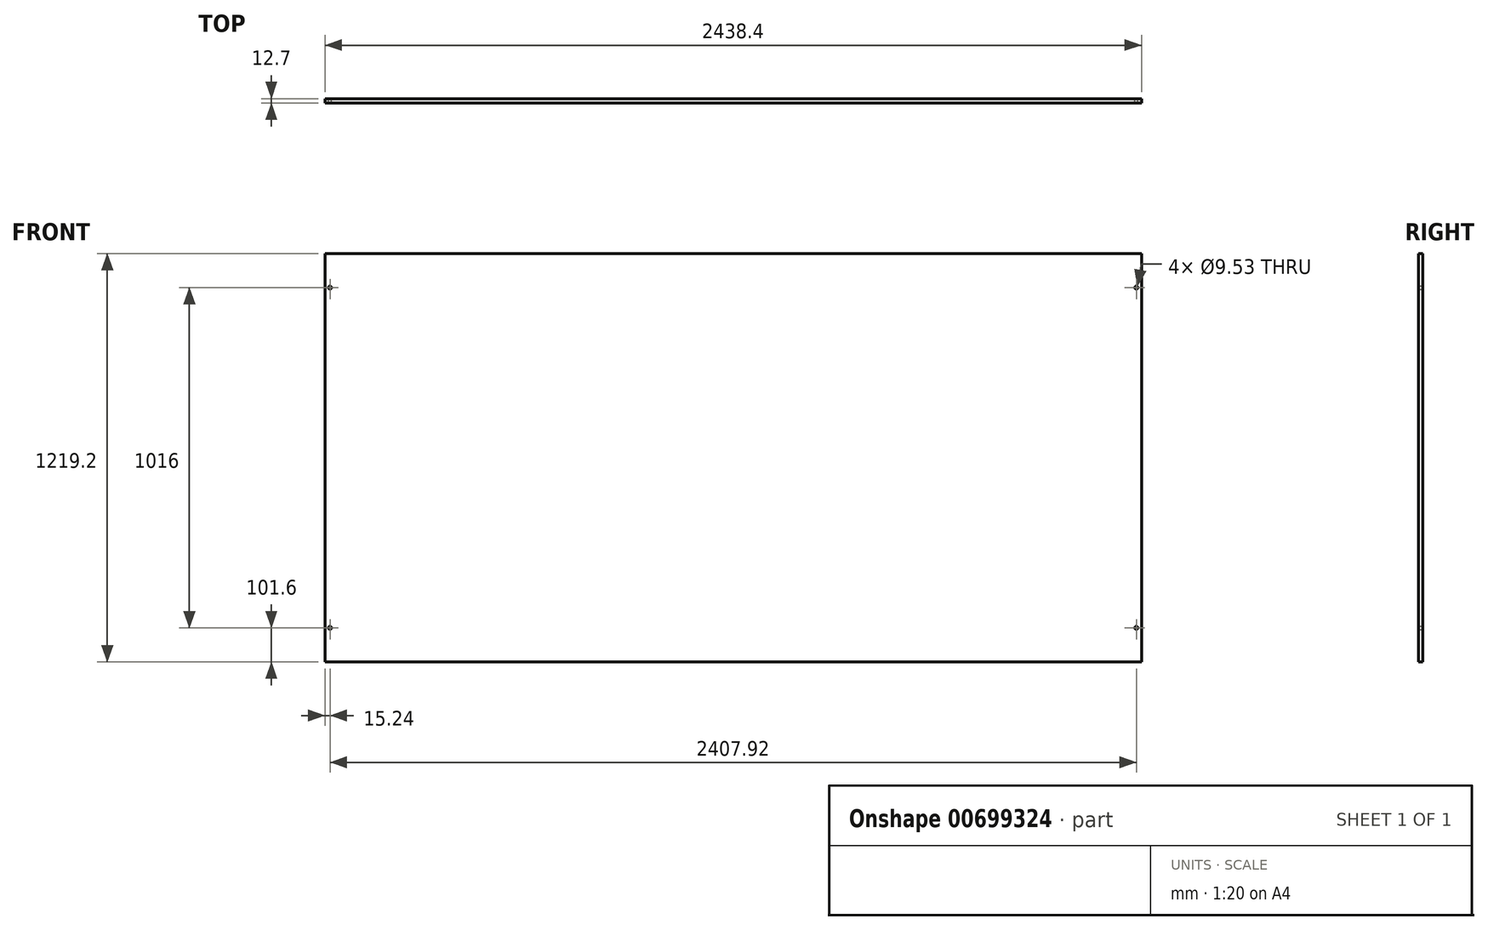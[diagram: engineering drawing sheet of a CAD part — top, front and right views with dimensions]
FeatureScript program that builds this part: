
annotation { "Feature Type Name" : "Feature", "Feature Type Description" : "" }
export const myFeature = defineFeature(function(context is Context, id is Id, definition is map)
    precondition{}
    {
        {
            var Q0;
            Q0=qCreatedBy(makeId("Front.planeOp"),FACE);
            var sketch = newSketch(context, id + "F0", { "sketchPlane" : qUnion([Q0])});
            skLineSegment(sketch, "E0.bottom", {"start": v(0, 0) * mm, "end": v(2438.4, 0) * mm});
            skLineSegment(sketch, "E0.top", {"start": v(0, 1219.2) * mm, "end": v(2438.4, 1219.2) * mm});
            skLineSegment(sketch, "E0.left", {"start": v(0, 0) * mm, "end": v(0, 1219.2) * mm});
            skLineSegment(sketch, "E0.right", {"start": v(2438.4, 0) * mm, "end": v(2438.4, 1219.2) * mm});
            skCircle(sketch, "E1", {"center": v(15.24, 1117.6) * mm, "radius": 4.76 * mm});
            skCircle(sketch, "E2", {"center": v(15.24, 101.6) * mm, "radius": 4.76 * mm});
            skCircle(sketch, "E3", {"center": v(2423.16, 1117.6) * mm, "radius": 4.76 * mm});
            skCircle(sketch, "E4", {"center": v(2423.16, 101.6) * mm, "radius": 4.76 * mm});
            skSolve(sketch);
        }
        {
            var Q0;
            Q0=makeQuery(id+"F0.imprint","IMPRINT",FACE,{"disambiguationData":[TD([[makeQuery(id+"F0.imprint","IMPRINT",EDGE,{"derivedFrom":sQuery(id+"F0.wireOp",EDGE,"E0.bottom")}),1.0]])]});
            extrude(context, id + "F1", {"entities" : qUnion([Q0]), "depth" : 12.7 * mm, "offsetDistance" : 25.4 * mm});
        }
    });
